# Revit family: QF_ELECTROLUXPROFESSIONAL_1LSNBN_IC64832LF_S
name_source: partatom
category: Attrezzature speciali
units: mm (PartAtom-declared; Revit-internal decimal feet)

## family parameters
Basato su piano di lavoro = No
Condiviso = No
Punto di calcolo locali = No
Quota connettore circolare = Usa diametro
Sempre verticale = Sì
Taglio con vuoti quando caricato = No
Tipo di parte = Normale

## types (6) — shared parameters
Depth Actual = 1110 mm
Height Actual = 1270 mm  [stored 4.16667 ft]
Latent Heat Output = 0.0
Length Actual = 3835 mm
Modello = IC64832LF
Phase = 3
Produttore = Electrolux Professional
Sensible Heat Output = 0.0
Steam Pounds per Hour = 141
URL = www.electroluxprofessional.com
Weight = 1015
zero-valued in all types: Gas KW, Prospetto di default

## per-type parameters (varying)
| type | Cycle | Descrizione | Item Number | Volts | Watts |
| 9882030059 | 50 Hz | IRONER CYLINDER IC64832LF LENGTH FOLDING 3170MM STEAM CE 400/50/3 4MM SST CYL. ML VAC.FEED.TABLE ANTISTATIC DIAMMS | 1LSP82 | 400 V | 3200 W |
| 9882030274 | 60 Hz | IRONER CYLINDER IC64832LF LENGTH FOLDING 3170MM ACTIVE STEAM CE 208-240/60/3 4MM SST CYL. EN, ES, PO | 1L0H8P | 240 V | 2000 W |
| 9882030227 | 60 Hz | IRONER CYLINDER IC64832LF LENGTH FOLDING 3170MM ACTIVE STEAM CE 480/60/3 4MM SST CYL. EN, ES, PO | 1LA23F | 480 V | 1400 W |
| 9882030259 | 50 Hz | IRONER CYLINDER IC64832LF LENGTH FOLDING 3170MM PERFORMANCE STEAM CE 400/50/3 4MM SST CYL. ML VAC.FEED.TABLE DIAMMS | 1L828V | 400 V | 3200 W |
| 9882030225 | 50 Hz | IRONER CYLINDER IC64832LF LENGTH FOLDING 3170MM STEAM CE 400/50/3 4MM SST CYL. ML DIAMMS | 1L827A | 400 V | 3200 W |
| 9882030283 | 50 Hz | IRONER CYLINDER IC64832LF LENGTH FOLDING 3170MM SUPERIOR STEAM CE 400/50/3 4MM SST CYL. FR FEED ALONE VAC.FEED.TABLE ANT | 1L0H53 | 400 V | 3200 W |

note: [stored X ft] marks values corroborated as IEEE doubles in the binary element streams (Revit-internal decimal feet)

## geometry (parser evidence)
native form markers: Sweep x11
no freeform markers — native parametric forms only
